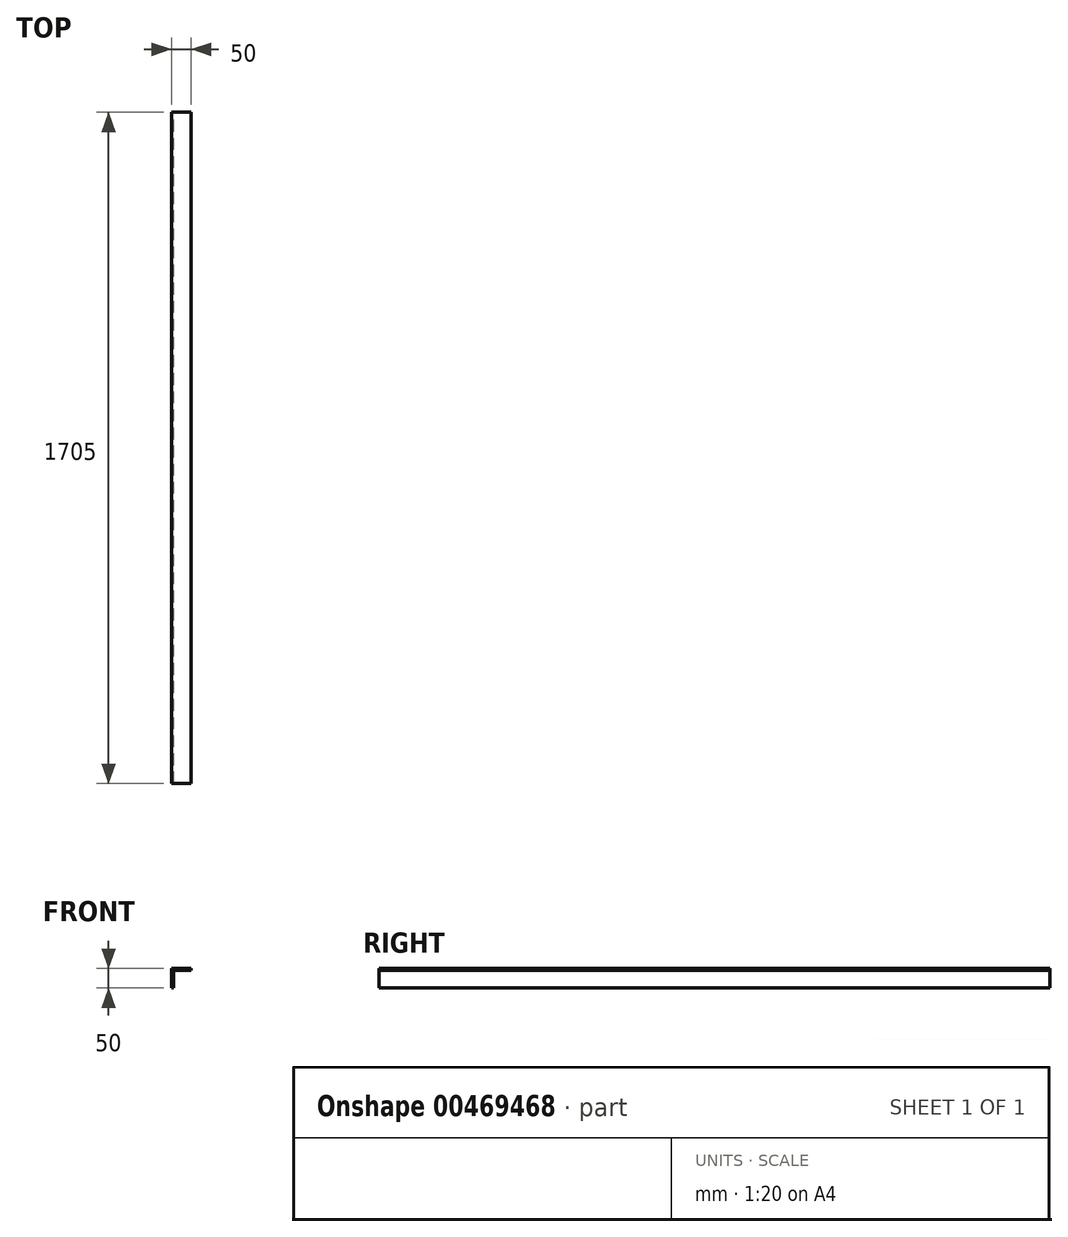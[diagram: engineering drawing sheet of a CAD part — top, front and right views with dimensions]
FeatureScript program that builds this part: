
annotation { "Feature Type Name" : "Feature", "Feature Type Description" : "" }
export const myFeature = defineFeature(function(context is Context, id is Id, definition is map)
    precondition{}
    {
        {
            var Q0;
            Q0=qCreatedBy(makeId("Front.planeOp"),FACE);
            var sketch = newSketch(context, id + "F0", { "sketchPlane" : qUnion([Q0])});
            skLineSegment(sketch, "E0", {"start": v(0, 0) * mm, "end": v(0, 50) * mm});
            skLineSegment(sketch, "E1", {"start": v(0, 50) * mm, "end": v(50, 50) * mm});
            skLineSegment(sketch, "E2", {"start": v(50, 50) * mm, "end": v(50, 45) * mm});
            skLineSegment(sketch, "E3", {"start": v(50, 45) * mm, "end": v(5, 45) * mm});
            skLineSegment(sketch, "E4", {"start": v(5, 45) * mm, "end": v(5, 0) * mm});
            skLineSegment(sketch, "E5", {"start": v(5, 0) * mm, "end": v(0, 0) * mm});
            skSolve(sketch);
        }
        {
            var Q0;
            Q0 = qSketchRegion(id + "F0", true);
            extrude(context, id + "F1", {"entities" : qUnion([Q0]), "depth" : 1705 * mm});
        }
    });
